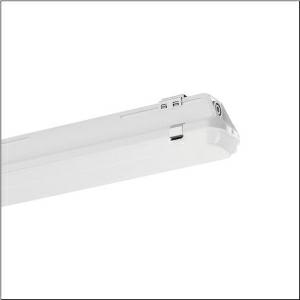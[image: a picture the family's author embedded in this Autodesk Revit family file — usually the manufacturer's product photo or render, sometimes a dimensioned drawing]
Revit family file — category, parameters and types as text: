
# Revit family: monsun_11_51fp20dp4b0u007
name_source: partatom
category: Lighting Fixtures
units: mm (PartAtom-declared; Revit-internal decimal feet)

## family parameters
Cut with Voids When Loaded = No
Host = Face
Light Source = No
Part Type = Normal
Room Calculation Point = No
Round Connector Dimension = Use Diameter
Shared = No

## types (1)
- --- (1 x LED, 10950 lm, 63.7 W, 4000K)
    Apparent Load = 64 VA
    CIE Flux Codes = 45 75 93 94 100
    Color Rendering = 80
    Color Temperature = 4000K
    Default Elevation = 1800 mm
    Description = Monsun 11, damp-proof luminaire, chain hanger, primary optical cover: enclosure, of PC, light emission: direct distribution, primary light characteristic: symmetric, installation type: suspended mounting, surface-mounted, horizontal mounting, vertical mounting, LED, rated luminous flux: 10.950lm, luminous efficacy: 172lm/W, light colour: 840, colour temperature: 4000K, control gear: DALI 2, with terminal, 5-pole, max. 2.5mm², through-wiring: 7x 2.5mm², mains connection: 220..240V, AC, 50/60Hz, rated input power: 64W, housing, of glass-fibre reinforced polyester, uncoated, bright grey, incl. chain hanger, length: 1.590mm, width: 90mm, height: 88mm, clip for enclosure, of stainless steel (V2A), ceiling mounting element, of stainless steel (V2A), chain hanger, of stainless steel (V2A), protection rating (complete): IP66, insulation class (complete): insulation class I (protective earthing), certification: CE, ENEC, VDE, UKCA, protection symbol: D, impact resistance: IK08, permissible operating ambient temperature: -40..+30°C, standard: EN 50419, EN 60598-2-1, contact your sales advisor before using the luminaires in applications with unclear chemical exposure, large temperature fluctuations or condensation-forming humidity, LABS conformity tested according to VDMA 24364:2018-05, no direct snow, no direct sun, no direct rain, for indoor or canopied outdoor use, corresponds to IFS (International Featured Standards) requirements for safety and quality in the food industry, packaging unit: 1 piece
    Height = 89 mm
    Lamp = 1 x LED
    Lamp Light Flux = 10950 lm
    Lamp Power = 63.7 W
    Lamp count = 1
    Length = 1590 mm
    Luminous efficacy = 172 lm/W
    Manufacturer = Siteco
    ModVariant = No
    Model = 51FP20DP4B0U007
    Mounting Place = Ceiling
    Mounting Type = Surface mounted
    Number of Poles = 1
    OnlyDefault = Yes
    Power Factor = 1
    Product Name = Monsun 11
    Product group = damp-proof luminaire
    ProductGroupID = 300
    Protection Class = Protection class I
    Protection Degree = IP 66
    RLX_Detail_Level = 1
    RLX_Emergency_Light_Flux = 0 lm
    RLX_Emergency_Type = 0
    RLX_Emergency_Type_DB = No
    RlxData = <blob elided: 92189 chars, md5=d727c5c1>
    Socket = socket
    Standby Power = 0 W
    System Light Flux = 10950 lm
    System Power = 64 W
    Type Comments = factory setting: luminous flux: 100 % | dim-lin: 254 | 441 mA
    Type Image = l_1349237.jpg
    URL = http://relux.com
    VarID = @adj_037763
    Voltage = 0 V
    Weight = 0.00 kg
    Width = 90 mm

## geometry (parser evidence)
native form markers: Blend x4, Sweep x13
no freeform markers — native parametric forms only
